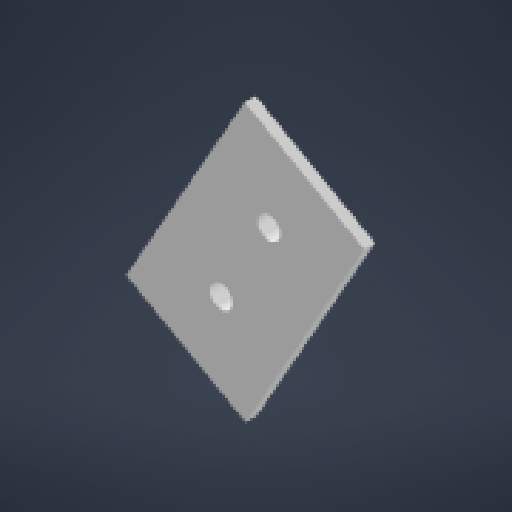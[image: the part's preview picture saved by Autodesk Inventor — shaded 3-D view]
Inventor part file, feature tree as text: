
AUTODESK INVENTOR PART (.ipt)
format: ipt  version: 2024.2 (Build 282272000, 272)  size: 214,016 bytes
history: native  units: in
note: dims shown in document units (in); Inventor stores cm internally (conversion verified against a paired STEP export)
features: extrude x9, sketch x9, fillet x5, other x5, projected_geometry x4, reference x3, plane x2
ambient origin geometry x8: Origin, YZ Plane, XZ Plane, XY Plane, X Axis, Y Axis, Z Axis, Center Point
bodies: Solid1 (feature_tree)
feature tree (37):
  extrude  "Extrusion1"  Depth=0.1575in TaperAngle=0.0deg
  plane  "Work Plane1"
  extrude  "Extrusion2"  Depth=2.0in
  extrude  "Extrusion3"  Depth=0.125in
  fillet  "Fillet1"  Radius=0.125in
  fillet  "Fillet2"  Radius=1.1866in
  extrude  "Extrusion4"  Depth=0.475in TaperAngle=0.0deg
  fillet  "Fillet3"  Radius=0.275in
  extrude  "Extrusion5"  Depth=0.315in TaperAngle=0.0deg
  extrude  "Extrusion6"  Depth=0.315in TaperAngle=0.0deg
  extrude  "Extrusion8"  Depth=0.125in TaperAngle=0.0deg
  fillet  "Fillet4"  Radius=0.125in
  plane  "Work Plane2"
  extrude  "Extrusion7"  [1 undecoded]
  extrude  "Extrusion9"  [1 undecoded]
  fillet  "Fillet5"  [1 undecoded]
  sketch  "Sketch1"  dims[d0=0.1575in d1=0.0in d2=0.1575in d3=0.0in]
  sketch  "Sketch2"  dims[d4=3.5in d5=2.0in]
  sketch  "Sketch3"  dims[d6=0.1575in d7=0.0in d8=0.125in d9=0.125in d10=1.1866in d11=0.0in]
  sketch  "Sketch4"  dims[d12=0.0156in d13=0.475in d14=0.0in d15=0.275in d16=0.0in]
  reference  "Reference1"
  reference  "Reference2"
  sketch  "Sketch5"  dims[d17=0.1496in d18=0.315in d19=0.0in]
  reference  "Reference3"
  sketch  "Sketch6"  dims[d20=0.1575in d21=0.315in d22=0.0in]
  projected_geometry  "Projected Loop1"
  sketch  "Sketch7"  dims[d23=0.0156in d24=0.0197in d25=0.0in d26=0.125in]
  projected_geometry  "Projected Loop2"
  sketch  "Sketch8"
  sketch  "Sketch9"
  projected_geometry  "Project Cut Edges1"
  projected_geometry  "Project Cut Edges2"
  other  "<userpath>\Desktop\Robotics\Cad\Powerplay_Fun\Parts\Claw_Assembly.iam"
  other  "Claw_Assembly.iam"
  other  "1611 Series Flanged Ball Bearing (8mm ID x 14mm OD, 5mm Thickness):2"
  other  "1611 Series Flanged Ball Bearing (8mm ID x 14mm OD, 5mm Thickness):3"
  other  "1611 Series Flanged Ball Bearing (8mm ID x 14mm OD, 5mm Thickness):1"
note: 3 required parameter values undecoded (feature->parameter linkage not recoverable at this tier; creation-order binding heuristic only, values carry confidence <= 0.55)
